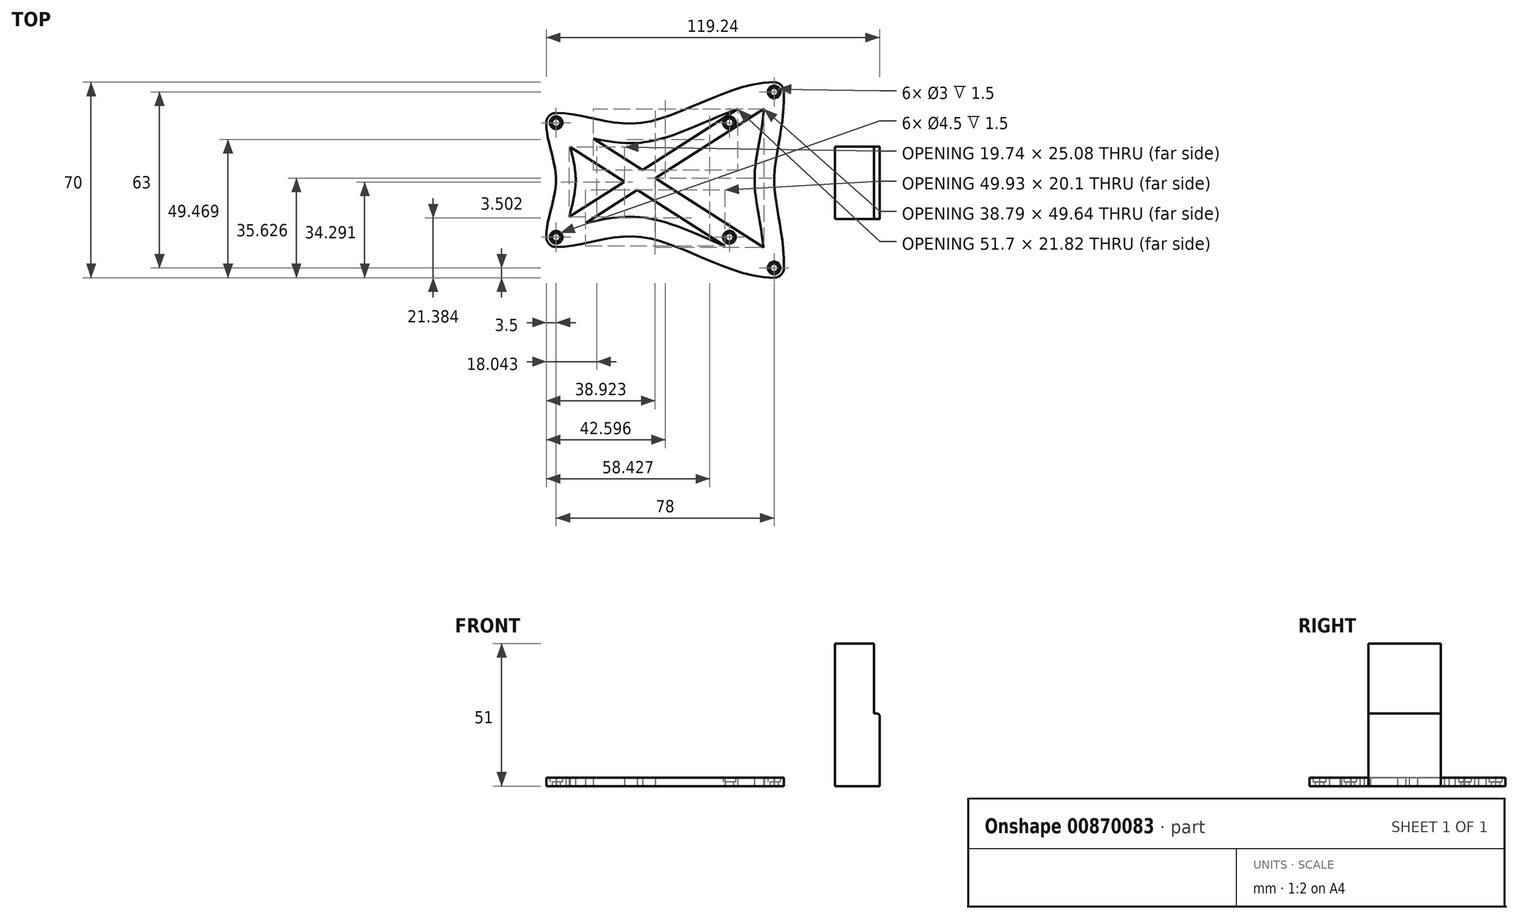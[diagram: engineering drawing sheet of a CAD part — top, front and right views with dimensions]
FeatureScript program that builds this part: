
annotation { "Feature Type Name" : "Feature", "Feature Type Description" : "" }
export const myFeature = defineFeature(function(context is Context, id is Id, definition is map)
    precondition{}
    {
        {
            var Q0;
            Q0=qCreatedBy(makeId("Top.planeOp"),FACE);
            var sketch = newSketch(context, id + "F0", { "sketchPlane" : qUnion([Q0])});
            skPoint(sketch, "E0.0.midPoint", {"position": v(0, 58.75) * mm});
            skLineSegment(sketch, "E1", {"start": v(-41.54, 41.54) * mm, "end": v(-31.58, 51.5) * mm});
            skLineSegment(sketch, "E2", {"start": v(-41.54, 41.54) * mm, "end": v(-51.5, 31.58) * mm});
            skPoint(sketch, "E3.center", {"position": v(0, 0) * mm});
            skLineSegment(sketch, "E4", {"start": v(0, 52.86) * mm, "end": v(0, 47.36) * mm, "construction": true});
            skArc(sketch, "E5.1.0", {"start": v(-52.21, -28.46) * mm, "mid": v(-47.36, 0) * mm, "end": v(-52.21, 28.46) * mm});
            skArc(sketch, "E6.1.0", {"start": v(28.46, -52.21) * mm, "mid": v(0, -47.36) * mm, "end": v(-28.46, -52.21) * mm});
            skArc(sketch, "E6.2.0", {"start": v(52.21, 28.46) * mm, "mid": v(47.36, 0) * mm, "end": v(52.21, -28.46) * mm});
            skArc(sketch, "E6.3.0", {"start": v(-28.46, 52.21) * mm, "mid": v(0, 47.36) * mm, "end": v(28.46, 52.21) * mm});
            skLineSegment(sketch, "E7.1.0", {"start": v(-41.54, -41.54) * mm, "end": v(-51.5, -31.58) * mm});
            skLineSegment(sketch, "E7.1.1", {"start": v(-41.54, -41.54) * mm, "end": v(-31.58, -51.5) * mm});
            skLineSegment(sketch, "E7.2.0", {"start": v(41.54, -41.54) * mm, "end": v(31.58, -51.5) * mm});
            skLineSegment(sketch, "E7.2.1", {"start": v(41.54, -41.54) * mm, "end": v(51.5, -31.58) * mm});
            skLineSegment(sketch, "E7.3.0", {"start": v(41.54, 41.54) * mm, "end": v(51.5, 31.58) * mm});
            skLineSegment(sketch, "E7.3.1", {"start": v(41.54, 41.54) * mm, "end": v(31.58, 51.5) * mm});
            skPoint(sketch, "E8.visualSharp", {"position": v(-52.86, 30.23) * mm});
            skArc(sketch, "E8.filletArc", {"start": v(-51.5, 31.58) * mm, "mid": v(-52.3, 30.12) * mm, "end": v(-52.21, 28.46) * mm});
            skPoint(sketch, "E9.visualSharp", {"position": v(-30.23, 52.86) * mm});
            skArc(sketch, "E9.filletArc", {"start": v(-28.46, 52.21) * mm, "mid": v(-30.12, 52.3) * mm, "end": v(-31.58, 51.5) * mm});
            skPoint(sketch, "E10.visualSharp", {"position": v(30.23, 52.86) * mm});
            skArc(sketch, "E10.filletArc", {"start": v(31.58, 51.5) * mm, "mid": v(30.12, 52.3) * mm, "end": v(28.46, 52.21) * mm});
            skPoint(sketch, "E11.visualSharp", {"position": v(52.86, 30.23) * mm});
            skArc(sketch, "E11.filletArc", {"start": v(52.21, 28.46) * mm, "mid": v(52.3, 30.12) * mm, "end": v(51.5, 31.58) * mm});
            skPoint(sketch, "E12.visualSharp", {"position": v(52.86, -30.23) * mm});
            skArc(sketch, "E12.filletArc", {"start": v(51.5, -31.58) * mm, "mid": v(52.3, -30.12) * mm, "end": v(52.21, -28.46) * mm});
            skPoint(sketch, "E13.visualSharp", {"position": v(30.23, -52.86) * mm});
            skArc(sketch, "E13.filletArc", {"start": v(28.46, -52.21) * mm, "mid": v(30.12, -52.3) * mm, "end": v(31.58, -51.5) * mm});
            skPoint(sketch, "E14.visualSharp", {"position": v(-30.23, -52.86) * mm});
            skArc(sketch, "E14.filletArc", {"start": v(-31.58, -51.5) * mm, "mid": v(-30.12, -52.3) * mm, "end": v(-28.46, -52.21) * mm});
            skPoint(sketch, "E15.visualSharp", {"position": v(-52.86, -30.23) * mm});
            skArc(sketch, "E15.filletArc", {"start": v(-52.21, -28.46) * mm, "mid": v(-52.3, -30.12) * mm, "end": v(-51.5, -31.58) * mm});
            skSolve(sketch);
        }
        {
            var Q0;
            Q0=makeQuery(id+"F0.imprint","IMPRINT",FACE,{"disambiguationData":[TD([[makeQuery(id+"F0.imprint","IMPRINT",EDGE,{"derivedFrom":sQuery(id+"F0.wireOp",EDGE,"E1")}),-1.0]])]});
            var sketch = newSketch(context, id + "F1", { "sketchPlane" : qUnion([Q0])});
            skLineSegment(sketch, "E16.bottom", {"start": v(92.64, 11.55) * mm, "end": v(108.64, 11.55) * mm});
            skLineSegment(sketch, "E16.top", {"start": v(92.64, -14.45) * mm, "end": v(108.64, -14.45) * mm});
            skLineSegment(sketch, "E16.left", {"start": v(92.64, 11.55) * mm, "end": v(92.64, -14.45) * mm});
            skLineSegment(sketch, "E16.right", {"start": v(108.64, 11.55) * mm, "end": v(108.64, -14.45) * mm});
            skSolve(sketch);
        }
        {
            var Q0;
            Q0=makeQuery(id+"F1.imprint","IMPRINT",FACE,{"disambiguationData":[TD([[makeQuery(id+"F1.imprint","IMPRINT",EDGE,{"derivedFrom":sQuery(id+"F1.wireOp",EDGE,"E16.bottom")}),-1.0]])]});
            extrude(context, id + "F2", {"entities" : qUnion([Q0]), "depth" : 26 * mm, "offsetDistance" : 25 * mm});
        }
        {
            var Q0;
            Q0=makeQuery(id+"F2.opExtrude","CAP_FACE",FACE,{"disambiguationData":[OSD([sQuery(id+"F1.wireOp",EDGE,"E16.bottom"),sQuery(id+"F1.wireOp",EDGE,"E16.top"),sQuery(id+"F1.wireOp",EDGE,"E16.left"),sQuery(id+"F1.wireOp",EDGE,"E16.right")])],"isStart":false});
            var sketch = newSketch(context, id + "F3", { "sketchPlane" : qUnion([Q0])});
            skLineSegment(sketch, "E17.bottom", {"start": v(92.64, 11.55) * mm, "end": v(106.64, 11.55) * mm});
            skLineSegment(sketch, "E17.top", {"start": v(92.64, -14.45) * mm, "end": v(106.64, -14.45) * mm});
            skLineSegment(sketch, "E17.left", {"start": v(92.64, 11.55) * mm, "end": v(92.64, -14.45) * mm});
            skLineSegment(sketch, "E17.right", {"start": v(106.64, 11.55) * mm, "end": v(106.64, -14.45) * mm});
            skSolve(sketch);
        }
        {
            var Q0;
            Q0=makeQuery(id+"F3.imprint","IMPRINT",FACE,{"disambiguationData":[TD([[makeQuery(id+"F3.imprint","IMPRINT",EDGE,{"derivedFrom":sQuery(id+"F3.wireOp",EDGE,"E17.bottom")}),-1.0]])]});
            extrude(context, id + "F4", {"entities" : qUnion([Q0]), "operationType" : NewBodyOperationType.ADD, "depth" : 25 * mm, "offsetDistance" : 25 * mm});
        }
        {
            var Q0;
            Q0=makeQuery(id+"F2.opExtrude","CAP_EDGE",EDGE,{"disambiguationData":[OSD([sQuery(id+"F1.wireOp",EDGE,"E16.right")])],"isStart":false});
            var Q1;
            Q1=makeQuery(id+"F4.opExtrude","CAP_EDGE",EDGE,{"disambiguationData":[OSD([sQuery(id+"F3.wireOp",EDGE,"E17.right")])],"isStart":true});
            fillet(context, id + "F5", {"entities" : qUnion([Q0, Q1]), "tangentPropagation" : true, "radius" : 1 * mm, "defaultsChanged" : true, "vertexSettings" : [], "allowEdgeOverflow" : false});
        }
        {
            var Q0;
            Q0=qCreatedBy(makeId("Top.planeOp"),FACE);
            var sketch = newSketch(context, id + "F6", { "sketchPlane" : qUnion([Q0])});
            skLineSegment(sketch, "E18.bottom", {"start": v(70.9, 31.08) * mm, "end": v(54.9, 31.08) * mm, "construction": true});
            skLineSegment(sketch, "E18.top", {"start": v(70.9, -31.92) * mm, "end": v(54.9, -31.92) * mm});
            skLineSegment(sketch, "E18.left", {"start": v(70.9, 31.08) * mm, "end": v(70.9, -31.92) * mm, "construction": true});
            skLineSegment(sketch, "E18.right", {"start": v(54.9, 31.08) * mm, "end": v(54.9, -31.92) * mm, "construction": true});
            skLineSegment(sketch, "E19", {"start": v(54.9, -31.92) * mm, "end": v(54.9, -20.92) * mm, "construction": true});
            skLineSegment(sketch, "E20", {"start": v(54.9, 31.08) * mm, "end": v(54.9, 20.08) * mm, "construction": true});
            skCircle(sketch, "E21", {"center": v(70.9, 31.08) * mm, "radius": 1.5 * mm});
            skCircle(sketch, "E22", {"center": v(70.9, 31.08) * mm, "radius": 2.25 * mm});
            skCircle(sketch, "E23", {"center": v(54.9, 20.08) * mm, "radius": 1.5 * mm});
            skCircle(sketch, "E24", {"center": v(54.9, 20.08) * mm, "radius": 2.25 * mm});
            skCircle(sketch, "E25", {"center": v(54.9, -20.92) * mm, "radius": 1.5 * mm});
            skCircle(sketch, "E26", {"center": v(54.9, -20.92) * mm, "radius": 2.25 * mm});
            skCircle(sketch, "E27", {"center": v(70.9, -31.92) * mm, "radius": 1.5 * mm});
            skCircle(sketch, "E28", {"center": v(70.9, -31.92) * mm, "radius": 2.25 * mm});
            skCircle(sketch, "E29", {"center": v(70.9, 31.08) * mm, "radius": 3.5 * mm});
            skCircle(sketch, "E30", {"center": v(70.9, -31.92) * mm, "radius": 3.5 * mm});
            skFitSpline(sketch, "E31", {"points": [v(74.4, 31.08) * mm, v(70.9, -0.42) * mm, v(74.4, -31.92) * mm], "startDerivative": vector(0, -88.08) * mm, "endDerivative": vector(0, -81.88) * mm});
            skLineSegment(sketch, "E32.bottom", {"start": v(54.9, 20.08) * mm, "end": v(-7.1, 20.08) * mm, "construction": true});
            skLineSegment(sketch, "E32.top", {"start": v(54.9, -20.92) * mm, "end": v(-7.1, -20.92) * mm, "construction": true});
            skLineSegment(sketch, "E32.right", {"start": v(-7.1, 20.08) * mm, "end": v(-7.1, -20.92) * mm, "construction": true});
            skCircle(sketch, "E33", {"center": v(-7.1, 20.08) * mm, "radius": 1.5 * mm});
            skCircle(sketch, "E34", {"center": v(-7.1, -20.92) * mm, "radius": 1.5 * mm});
            skCircle(sketch, "E35", {"center": v(-7.1, 20.08) * mm, "radius": 2.25 * mm});
            skCircle(sketch, "E36", {"center": v(-7.1, -20.92) * mm, "radius": 2.25 * mm});
            skCircle(sketch, "E37", {"center": v(-7.1, 20.08) * mm, "radius": 3.5 * mm});
            skCircle(sketch, "E38", {"center": v(-7.1, -20.92) * mm, "radius": 3.5 * mm});
            skFitSpline(sketch, "E39", {"points": [v(-10.6, 20.08) * mm, v(-7.1, -0.42) * mm, v(-10.6, -20.92) * mm], "startDerivative": vector(0, -42.32) * mm, "endDerivative": vector(0, -42.32) * mm});
            skFitSpline(sketch, "E40", {"points": [v(-7.1, -24.42) * mm, v(23.9, -20.92) * mm, v(70.9, -35.42) * mm], "startDerivative": vector(67.67, 0) * mm, "endDerivative": vector(86.23, 0) * mm});
            skFitSpline(sketch, "E41", {"points": [v(-7.1, 23.58) * mm, v(23.9, 20.08) * mm, v(70.9, 34.58) * mm], "startDerivative": vector(68.47, 0) * mm, "endDerivative": vector(86.23, 0) * mm});
            skLineSegment(sketch, "E42", {"start": v(-7.1, -20.92) * mm, "end": v(2.9, -20.92) * mm, "construction": true});
            skLineSegment(sketch, "E43", {"start": v(2.9, -20.92) * mm, "end": v(2.9, 20.08) * mm, "construction": true});
            skFitSpline(sketch, "E44.0", {"points": [v(-7.1, 16.58) * mm, v(-6.55, 16.58) * mm, v(-5.44, 16.54) * mm, v(-3.7, 16.38) * mm, v(-1.87, 16.12) * mm, v(0.04, 15.77) * mm, v(2.04, 15.36) * mm, v(4.12, 14.9) * mm, v(6.3, 14.43) * mm, v(8.56, 13.96) * mm, v(10.93, 13.53) * mm, v(13.4, 13.16) * mm, v(15.54, 12.93) * mm, v(17.31, 12.82) * mm, v(18.67, 12.77) * mm, v(20.05, 12.77) * mm, v(21.45, 12.82) * mm, v(22.64, 12.9) * mm, v(23.6, 13) * mm, v(24.2, 13.06) * mm, v(24.7, 13.12) * mm, v(25.18, 13.2) * mm, v(25.8, 13.29) * mm, v(26.52, 13.41) * mm, v(27.48, 13.6) * mm, v(28.68, 13.86) * mm, v(30.1, 14.22) * mm, v(31.52, 14.62) * mm, v(33.39, 15.19) * mm, v(35.7, 15.98) * mm, v(38.45, 17.01) * mm, v(41.17, 18.11) * mm, v(43.87, 19.25) * mm, v(47.44, 20.78) * mm, v(51.84, 22.66) * mm, v(56.13, 24.35) * mm, v(59.46, 25.5) * mm, v(61.9, 26.22) * mm, v(64.28, 26.82) * mm, v(66.58, 27.25) * mm, v(68.8, 27.52) * mm, v(70.2, 27.58) * mm, v(70.9, 27.58) * mm]});
            skFitSpline(sketch, "E45.0", {"points": [v(-7.1, -17.42) * mm, v(-6.56, -17.42) * mm, v(-5.46, -17.38) * mm, v(-3.74, -17.21) * mm, v(-1.92, -16.95) * mm, v(-0.02, -16.6) * mm, v(1.97, -16.2) * mm, v(4.06, -15.74) * mm, v(6.24, -15.27) * mm, v(8.51, -14.8) * mm, v(10.89, -14.36) * mm, v(13.36, -14) * mm, v(15.52, -13.77) * mm, v(17.3, -13.66) * mm, v(18.65, -13.61) * mm, v(20.03, -13.6) * mm, v(21.44, -13.65) * mm, v(22.63, -13.73) * mm, v(23.6, -13.83) * mm, v(24.2, -13.9) * mm, v(24.69, -13.96) * mm, v(25.18, -14.03) * mm, v(25.79, -14.12) * mm, v(26.52, -14.25) * mm, v(27.48, -14.44) * mm, v(28.68, -14.7) * mm, v(30.11, -15.06) * mm, v(31.53, -15.45) * mm, v(33.4, -16.02) * mm, v(35.72, -16.81) * mm, v(38.47, -17.85) * mm, v(41.2, -18.95) * mm, v(43.9, -20.09) * mm, v(47.46, -21.62) * mm, v(51.86, -23.5) * mm, v(56.14, -25.19) * mm, v(59.47, -26.33) * mm, v(61.9, -27.06) * mm, v(64.28, -27.65) * mm, v(66.58, -28.09) * mm, v(68.8, -28.36) * mm, v(70.2, -28.42) * mm, v(70.9, -28.42) * mm]});
            skFitSpline(sketch, "E46.0", {"points": [v(-3.6, 20.08) * mm, v(-3.6, 19.79) * mm, v(-3.58, 19.18) * mm, v(-3.5, 18.22) * mm, v(-3.37, 17.22) * mm, v(-3.12, 15.81) * mm, v(-2.7, 13.93) * mm, v(-2.18, 11.9) * mm, v(-1.74, 10.16) * mm, v(-1.4, 8.82) * mm, v(-1.07, 7.42) * mm, v(-0.77, 5.98) * mm, v(-0.54, 4.72) * mm, v(-0.4, 3.69) * mm, v(-0.3, 2.9) * mm, v(-0.2, 2.1) * mm, v(-0.16, 1.4) * mm, v(-0.13, 0.85) * mm, v(-0.11, 0.43) * mm, v(-0.1, 0.08) * mm, v(-0.1, -0.2) * mm, v(-0.1, -0.42) * mm, v(-0.1, -0.63) * mm, v(-0.1, -0.92) * mm, v(-0.11, -1.27) * mm, v(-0.13, -1.69) * mm, v(-0.16, -2.24) * mm, v(-0.2, -2.93) * mm, v(-0.3, -3.73) * mm, v(-0.4, -4.52) * mm, v(-0.54, -5.56) * mm, v(-0.77, -6.81) * mm, v(-1.08, -8.26) * mm, v(-1.4, -9.66) * mm, v(-1.74, -11) * mm, v(-2.18, -12.73) * mm, v(-2.7, -14.77) * mm, v(-3.12, -16.65) * mm, v(-3.37, -18.05) * mm, v(-3.5, -19.06) * mm, v(-3.58, -20.02) * mm, v(-3.6, -20.62) * mm, v(-3.6, -20.92) * mm]});
            skFitSpline(sketch, "E47.0", {"points": [v(67.4, 31.08) * mm, v(67.4, 29.39) * mm, v(67.3, 26.2) * mm, v(66.92, 21.9) * mm, v(66.39, 17.96) * mm, v(65.87, 14.89) * mm, v(65.43, 12.5) * mm, v(65.11, 10.7) * mm, v(64.8, 8.92) * mm, v(64.52, 7.13) * mm, v(64.3, 5.6) * mm, v(64.17, 4.38) * mm, v(64.07, 3.44) * mm, v(64, 2.5) * mm, v(63.95, 1.7) * mm, v(63.93, 1.05) * mm, v(63.91, 0.57) * mm, v(63.9, 0.16) * mm, v(63.9, -0.17) * mm, v(63.9, -0.42) * mm, v(63.9, -0.67) * mm, v(63.9, -1) * mm, v(63.91, -1.4) * mm, v(63.93, -1.9) * mm, v(63.95, -2.54) * mm, v(64, -3.35) * mm, v(64.07, -4.3) * mm, v(64.16, -5.26) * mm, v(64.3, -6.51) * mm, v(64.51, -8.07) * mm, v(64.8, -9.93) * mm, v(65.1, -11.77) * mm, v(65.43, -13.62) * mm, v(65.86, -16.1) * mm, v(66.39, -19.26) * mm, v(66.92, -23.2) * mm, v(67.3, -27.38) * mm, v(67.4, -30.36) * mm, v(67.4, -31.92) * mm]});
            skLineSegment(sketch, "E48", {"start": v(-3.2, -17.13) * mm, "end": v(65.83, 27.1) * mm, "construction": true});
            skArc(sketch, "E49.0.startCap", {"start": v(-1.85, -19.24) * mm, "mid": v(-5.3, -18.48) * mm, "end": v(-4.55, -15.03) * mm, "construction": true});
            skArc(sketch, "E49.0.endCap", {"start": v(64.48, 29.2) * mm, "mid": v(67.93, 28.45) * mm, "end": v(67.17, 25) * mm});
            skLineSegment(sketch, "E49.0.left", {"start": v(-4.55, -15.03) * mm, "end": v(64.48, 29.2) * mm});
            skLineSegment(sketch, "E49.0.right", {"start": v(-1.85, -19.24) * mm, "end": v(67.17, 25) * mm});
            skLineSegment(sketch, "E50", {"start": v(-3.2, 16.3) * mm, "end": v(65.75, -27.93) * mm, "construction": true});
            skArc(sketch, "E51.0.startCap", {"start": v(-5.1, 13.36) * mm, "mid": v(-6.15, 18.2) * mm, "end": v(-1.31, 19.25) * mm, "construction": true});
            skArc(sketch, "E51.0.endCap", {"start": v(67.64, -24.98) * mm, "mid": v(68.7, -29.81) * mm, "end": v(63.87, -30.87) * mm, "construction": true});
            skLineSegment(sketch, "E51.0.left", {"start": v(-1.31, 19.25) * mm, "end": v(67.64, -24.98) * mm});
            skLineSegment(sketch, "E51.0.right", {"start": v(-5.1, 13.36) * mm, "end": v(63.87, -30.87) * mm});
            skSolve(sketch);
        }
        {
            var Q0;
            {var subQ5=sQuery(id+"F6.wireOp",EDGE,"E39");Q0=makeQuery(id+"F6.imprint","IMPRINT",FACE,{"disambiguationData":[TD([[makeQuery(id+"F6.imprint","IMPRINT",EDGE,{"derivedFrom":subQ5}),1.0]])]});}
            var Q1;
            Q1=makeQuery(id+"F6.imprint","IMPRINT",FACE,{"disambiguationData":[TD([[makeQuery(id+"F6.imprint","IMPRINT",EDGE,{"derivedFrom":sQuery(id+"F6.wireOp",EDGE,"E36")}),-1.0]])]});
            var Q2;
            Q2=makeQuery(id+"F6.imprint","IMPRINT",FACE,{"disambiguationData":[TD([[makeQuery(id+"F6.imprint","IMPRINT",EDGE,{"derivedFrom":sQuery(id+"F6.wireOp",EDGE,"E34")}),-1.0]])]});
            var Q3;
            Q3=makeQuery(id+"F6.imprint","IMPRINT",FACE,{"disambiguationData":[TD([[makeQuery(id+"F6.imprint","IMPRINT",EDGE,{"derivedFrom":sQuery(id+"F6.wireOp",EDGE,"E27")}),-1.0]])]});
            var Q4;
            Q4=makeQuery(id+"F6.imprint","IMPRINT",FACE,{"disambiguationData":[TD([[makeQuery(id+"F6.imprint","IMPRINT",EDGE,{"derivedFrom":sQuery(id+"F6.wireOp",EDGE,"E28")}),-1.0]])]});
            var Q5;
            Q5=makeQuery(id+"F6.imprint","IMPRINT",FACE,{"disambiguationData":[TD([[makeQuery(id+"F6.imprint","IMPRINT",EDGE,{"derivedFrom":sQuery(id+"F6.wireOp",EDGE,"E25")}),-1.0]])]});
            var Q6;
            Q6=makeQuery(id+"F6.imprint","IMPRINT",FACE,{"disambiguationData":[TD([[makeQuery(id+"F6.imprint","IMPRINT",EDGE,{"derivedFrom":sQuery(id+"F6.wireOp",EDGE,"E22")}),-1.0]])]});
            var Q7;
            Q7=makeQuery(id+"F6.imprint","IMPRINT",FACE,{"disambiguationData":[TD([[makeQuery(id+"F6.imprint","IMPRINT",EDGE,{"derivedFrom":sQuery(id+"F6.wireOp",EDGE,"E21")}),-1.0]])]});
            var Q8;
            Q8=makeQuery(id+"F6.imprint","IMPRINT",FACE,{"disambiguationData":[TD([[makeQuery(id+"F6.imprint","IMPRINT",EDGE,{"derivedFrom":sQuery(id+"F6.wireOp",EDGE,"E33")}),-1.0]])]});
            var Q9;
            Q9=makeQuery(id+"F6.imprint","IMPRINT",FACE,{"disambiguationData":[TD([[makeQuery(id+"F6.imprint","IMPRINT",EDGE,{"derivedFrom":sQuery(id+"F6.wireOp",EDGE,"E35")}),-1.0]])]});
            var Q10;
            Q10=makeQuery(id+"F6.imprint","IMPRINT",FACE,{"disambiguationData":[TD([[makeQuery(id+"F6.imprint","IMPRINT",EDGE,{"derivedFrom":sQuery(id+"F6.wireOp",EDGE,"E23")}),-1.0]])]});
            var Q11;
            {var subQ4=sQuery(id+"F6.wireOp",EDGE,"E40");var subQ5=sQuery(id+"F6.wireOp",EDGE,"E30");var subQ6=makeQuery(id+"F6.imprint","INTERSECT",VERTEX,{"derivedFrom":[subQ5,subQ4]});Q11=makeQuery(id+"F6.imprint","IMPRINT",FACE,{"disambiguationData":[TD([[makeQuery(id+"F6.imprint","IMPRINT",EDGE,{"disambiguationData":[TD([[subQ6,1.0]])],"derivedFrom":subQ5}),-1.0]])]});}
            var Q12;
            {var subQ4=sQuery(id+"F6.wireOp",EDGE,"E40");var subQ8=sQuery(id+"F6.wireOp",EDGE,"E38");var subQ9=makeQuery(id+"F6.imprint","INTERSECT",VERTEX,{"derivedFrom":[subQ8,subQ4]});Q12=makeQuery(id+"F6.imprint","IMPRINT",FACE,{"disambiguationData":[TD([[makeQuery(id+"F6.imprint","IMPRINT",EDGE,{"disambiguationData":[TD([[subQ9,-1.0]])],"derivedFrom":subQ8}),-1.0]])]});}
            var Q13;
            {var subQ0=sQuery(id+"F6.wireOp",EDGE,"E49.0.left");var subQ1=sQuery(id+"F6.wireOp",EDGE,"9af11305-70bc-4bd8-85a8-762773eb8b53.0.left");var subQ2=makeQuery(id+"F6.imprint","INTERSECT",VERTEX,{"derivedFrom":[subQ1,subQ0]});Q13=makeQuery(id+"F6.imprint","IMPRINT",FACE,{"disambiguationData":[TD([[makeQuery(id+"F6.imprint","IMPRINT",EDGE,{"disambiguationData":[TD([[subQ2,-1.0]])],"derivedFrom":subQ1}),-1.0]])]});}
            var Q14;
            {var subQ7=sQuery(id+"F6.wireOp",EDGE,"9af11305-70bc-4bd8-85a8-762773eb8b53.0.right");var subQ9=sQuery(id+"F6.wireOp",EDGE,"E26");var subQ11=makeQuery(id+"F6.imprint","INTERSECT",VERTEX,{"disambiguationData":[OD(0.0)],"derivedFrom":[subQ9,subQ7]});Q14=makeQuery(id+"F6.imprint","IMPRINT",FACE,{"disambiguationData":[TD([[makeQuery(id+"F6.imprint","IMPRINT",EDGE,{"disambiguationData":[TD([[subQ11,1.0]])],"derivedFrom":subQ9}),-1.0]])]});}
            var Q15;
            {var subQ5=sQuery(id+"F6.wireOp",EDGE,"E31");Q15=makeQuery(id+"F6.imprint","IMPRINT",FACE,{"disambiguationData":[TD([[makeQuery(id+"F6.imprint","IMPRINT",EDGE,{"derivedFrom":subQ5}),-1.0]])]});}
            var Q16;
            {var subQ0=sQuery(id+"F6.wireOp",EDGE,"E45.0");var subQ1=sQuery(id+"F6.wireOp",EDGE,"E30");var subQ2=makeQuery(id+"F6.imprint","INTERSECT",VERTEX,{"derivedFrom":[subQ1,subQ0]});Q16=makeQuery(id+"F6.imprint","IMPRINT",FACE,{"disambiguationData":[TD([[makeQuery(id+"F6.imprint","IMPRINT",EDGE,{"disambiguationData":[TD([[subQ2,-1.0]])],"derivedFrom":subQ1}),-1.0]])]});}
            var Q17;
            {var subQ6=sQuery(id+"F6.wireOp",EDGE,"E41");var subQ7=sQuery(id+"F6.wireOp",EDGE,"E29");var subQ8=makeQuery(id+"F6.imprint","INTERSECT",VERTEX,{"derivedFrom":[subQ7,subQ6]});Q17=makeQuery(id+"F6.imprint","IMPRINT",FACE,{"disambiguationData":[TD([[makeQuery(id+"F6.imprint","IMPRINT",EDGE,{"disambiguationData":[TD([[subQ8,-1.0]])],"derivedFrom":subQ7}),-1.0]])]});}
            var Q18;
            {var subQ0=sQuery(id+"F6.wireOp",EDGE,"E44.0");var subQ1=sQuery(id+"F6.wireOp",EDGE,"E29");var subQ2=makeQuery(id+"F6.imprint","INTERSECT",VERTEX,{"derivedFrom":[subQ1,subQ0]});Q18=makeQuery(id+"F6.imprint","IMPRINT",FACE,{"disambiguationData":[TD([[makeQuery(id+"F6.imprint","IMPRINT",EDGE,{"disambiguationData":[TD([[subQ2,1.0]])],"derivedFrom":subQ1}),-1.0]])]});}
            var Q19;
            {var subQ0=sQuery(id+"F6.wireOp",EDGE,"E49.0.right");var subQ1=sQuery(id+"F6.wireOp",EDGE,"9af11305-70bc-4bd8-85a8-762773eb8b53.0.left");var subQ2=makeQuery(id+"F6.imprint","INTERSECT",VERTEX,{"derivedFrom":[subQ1,subQ0]});Q19=makeQuery(id+"F6.imprint","IMPRINT",FACE,{"disambiguationData":[TD([[makeQuery(id+"F6.imprint","IMPRINT",EDGE,{"disambiguationData":[TD([[subQ2,-1.0]])],"derivedFrom":subQ1}),-1.0]])]});}
            var Q20;
            {var subQ0=sQuery(id+"F6.wireOp",EDGE,"E49.0.left");var subQ1=sQuery(id+"F6.wireOp",EDGE,"9af11305-70bc-4bd8-85a8-762773eb8b53.0.left");var subQ2=makeQuery(id+"F6.imprint","INTERSECT",VERTEX,{"derivedFrom":[subQ1,subQ0]});Q20=makeQuery(id+"F6.imprint","IMPRINT",FACE,{"disambiguationData":[TD([[makeQuery(id+"F6.imprint","IMPRINT",EDGE,{"disambiguationData":[TD([[subQ2,-1.0]])],"derivedFrom":subQ1}),1.0]])]});}
            var Q21;
            {var subQ4=sQuery(id+"F6.wireOp",EDGE,"E37");var subQ6=sQuery(id+"F6.wireOp",EDGE,"E41");var subQ7=makeQuery(id+"F6.imprint","INTERSECT",VERTEX,{"derivedFrom":[subQ4,subQ6]});Q21=makeQuery(id+"F6.imprint","IMPRINT",FACE,{"disambiguationData":[TD([[makeQuery(id+"F6.imprint","IMPRINT",EDGE,{"disambiguationData":[TD([[subQ7,1.0]])],"derivedFrom":subQ4}),-1.0]])]});}
            var Q22;
            {var subQ0=sQuery(id+"F6.wireOp",EDGE,"E44.0");var subQ1=sQuery(id+"F6.wireOp",EDGE,"E37");var subQ2=makeQuery(id+"F6.imprint","INTERSECT",VERTEX,{"derivedFrom":[subQ1,subQ0]});Q22=makeQuery(id+"F6.imprint","IMPRINT",FACE,{"disambiguationData":[TD([[makeQuery(id+"F6.imprint","IMPRINT",EDGE,{"disambiguationData":[TD([[subQ2,-1.0]])],"derivedFrom":subQ1}),-1.0]])]});}
            var Q23;
            {var subQ0=sQuery(id+"F6.wireOp",EDGE,"E45.0");var subQ1=sQuery(id+"F6.wireOp",EDGE,"E38");var subQ2=makeQuery(id+"F6.imprint","INTERSECT",VERTEX,{"derivedFrom":[subQ1,subQ0]});Q23=makeQuery(id+"F6.imprint","IMPRINT",FACE,{"disambiguationData":[TD([[makeQuery(id+"F6.imprint","IMPRINT",EDGE,{"disambiguationData":[TD([[subQ2,1.0]])],"derivedFrom":subQ1}),-1.0]])]});}
            var Q24;
            {var subQ3=sQuery(id+"F6.wireOp",EDGE,"E45.0");var subQ7=sQuery(id+"F6.wireOp",EDGE,"E49.0.right");var subQ9=makeQuery(id+"F6.imprint","INTERSECT",VERTEX,{"derivedFrom":[subQ3,subQ7]});Q24=makeQuery(id+"F6.imprint","IMPRINT",FACE,{"disambiguationData":[TD([[makeQuery(id+"F6.imprint","IMPRINT",EDGE,{"disambiguationData":[TD([[subQ9,1.0]])],"derivedFrom":subQ3}),1.0]])]});}
            var Q25;
            {var subQ0=sQuery(id+"F6.wireOp",EDGE,"E51.0.right");var subQ1=sQuery(id+"F6.wireOp",EDGE,"E49.0.right");var subQ2=makeQuery(id+"F6.imprint","INTERSECT",VERTEX,{"derivedFrom":[subQ1,subQ0]});Q25=makeQuery(id+"F6.imprint","IMPRINT",FACE,{"disambiguationData":[TD([[makeQuery(id+"F6.imprint","IMPRINT",EDGE,{"disambiguationData":[TD([[subQ2,-1.0]])],"derivedFrom":subQ1}),-1.0]])]});}
            var Q26;
            {var subQ0=sQuery(id+"F6.wireOp",EDGE,"E51.0.right");var subQ1=sQuery(id+"F6.wireOp",EDGE,"E49.0.left");var subQ2=makeQuery(id+"F6.imprint","INTERSECT",VERTEX,{"derivedFrom":[subQ1,subQ0]});Q26=makeQuery(id+"F6.imprint","IMPRINT",FACE,{"disambiguationData":[TD([[makeQuery(id+"F6.imprint","IMPRINT",EDGE,{"disambiguationData":[TD([[subQ2,-1.0]])],"derivedFrom":subQ1}),-1.0]])]});}
            var Q27;
            {var subQ3=sQuery(id+"F6.wireOp",EDGE,"E51.0.left");var subQ5=sQuery(id+"F6.wireOp",EDGE,"E44.0");var subQ6=makeQuery(id+"F6.imprint","INTERSECT",VERTEX,{"derivedFrom":[subQ5,subQ3]});Q27=makeQuery(id+"F6.imprint","IMPRINT",FACE,{"disambiguationData":[TD([[makeQuery(id+"F6.imprint","IMPRINT",EDGE,{"disambiguationData":[TD([[subQ6,1.0]])],"derivedFrom":subQ5}),-1.0]])]});}
            var Q28;
            {var subQ0=sQuery(id+"F6.wireOp",EDGE,"E51.0.left");var subQ1=sQuery(id+"F6.wireOp",EDGE,"E49.0.left");var subQ2=makeQuery(id+"F6.imprint","INTERSECT",VERTEX,{"derivedFrom":[subQ1,subQ0]});Q28=makeQuery(id+"F6.imprint","IMPRINT",FACE,{"disambiguationData":[TD([[makeQuery(id+"F6.imprint","IMPRINT",EDGE,{"disambiguationData":[TD([[subQ2,-1.0]])],"derivedFrom":subQ1}),-1.0]])]});}
            var Q29;
            Q29=makeQuery(id+"F6.imprint","IMPRINT",FACE,{"disambiguationData":[TD([[makeQuery(id+"F6.imprint","IMPRINT",EDGE,{"derivedFrom":sQuery(id+"F6.wireOp",EDGE,"E24")}),-1.0]])]});
            var Q30;
            {var subQ0=sQuery(id+"F6.wireOp",EDGE,"E49.0.left");var subQ1=sQuery(id+"F6.wireOp",EDGE,"E44.0");var subQ2=makeQuery(id+"F6.imprint","INTERSECT",VERTEX,{"derivedFrom":[subQ1,subQ0]});Q30=makeQuery(id+"F6.imprint","IMPRINT",FACE,{"disambiguationData":[TD([[makeQuery(id+"F6.imprint","IMPRINT",EDGE,{"disambiguationData":[TD([[subQ2,-1.0]])],"derivedFrom":subQ1}),1.0]])]});}
            var Q31;
            {var subQ0=sQuery(id+"F6.wireOp",EDGE,"E47.0");var subQ1=sQuery(id+"F6.wireOp",EDGE,"E44.0");var subQ2=makeQuery(id+"F6.imprint","INTERSECT",VERTEX,{"derivedFrom":[subQ1,subQ0]});Q31=makeQuery(id+"F6.imprint","IMPRINT",FACE,{"disambiguationData":[TD([[makeQuery(id+"F6.imprint","IMPRINT",EDGE,{"disambiguationData":[TD([[subQ2,-1.0]])],"derivedFrom":subQ1}),-1.0]])]});}
            var Q32;
            {var subQ0=sQuery(id+"F6.wireOp",EDGE,"E47.0");var subQ1=sQuery(id+"F6.wireOp",EDGE,"E44.0");var subQ2=makeQuery(id+"F6.imprint","INTERSECT",VERTEX,{"derivedFrom":[subQ1,subQ0]});Q32=makeQuery(id+"F6.imprint","IMPRINT",FACE,{"disambiguationData":[TD([[makeQuery(id+"F6.imprint","IMPRINT",EDGE,{"disambiguationData":[TD([[subQ2,-1.0]])],"derivedFrom":subQ1}),1.0]])]});}
            extrude(context, id + "F7", {"entities" : qUnion([Q0, Q1, Q2, Q3, Q4, Q5, Q6, Q7, Q8, Q9, Q10, Q11, Q12, Q13, Q14, Q15, Q16, Q17, Q18, Q19, Q20, Q21, Q22, Q23, Q24, Q25, Q26, Q27, Q28, Q29, Q30, Q31, Q32]), "operationType" : NewBodyOperationType.ADD, "depth" : 1.5 * mm, "offsetDistance" : 25 * mm});
        }
        {
            var Q0;
            {var subQ5=sQuery(id+"F6.wireOp",EDGE,"E31");Q0=makeQuery(id+"F6.imprint","IMPRINT",FACE,{"disambiguationData":[TD([[makeQuery(id+"F6.imprint","IMPRINT",EDGE,{"derivedFrom":subQ5}),-1.0]])]});}
            var Q1;
            {var subQ0=sQuery(id+"F6.wireOp",EDGE,"E45.0");var subQ1=sQuery(id+"F6.wireOp",EDGE,"E30");var subQ2=makeQuery(id+"F6.imprint","INTERSECT",VERTEX,{"derivedFrom":[subQ1,subQ0]});Q1=makeQuery(id+"F6.imprint","IMPRINT",FACE,{"disambiguationData":[TD([[makeQuery(id+"F6.imprint","IMPRINT",EDGE,{"disambiguationData":[TD([[subQ2,-1.0]])],"derivedFrom":subQ1}),-1.0]])]});}
            var Q2;
            {var subQ4=sQuery(id+"F6.wireOp",EDGE,"E40");var subQ8=sQuery(id+"F6.wireOp",EDGE,"E30");var subQ9=makeQuery(id+"F6.imprint","INTERSECT",VERTEX,{"derivedFrom":[subQ8,subQ4]});Q2=makeQuery(id+"F6.imprint","IMPRINT",FACE,{"disambiguationData":[TD([[makeQuery(id+"F6.imprint","IMPRINT",EDGE,{"disambiguationData":[TD([[subQ9,1.0]])],"derivedFrom":subQ8}),-1.0]])]});}
            var Q3;
            Q3=makeQuery(id+"F6.imprint","IMPRINT",FACE,{"disambiguationData":[TD([[makeQuery(id+"F6.imprint","IMPRINT",EDGE,{"derivedFrom":sQuery(id+"F6.wireOp",EDGE,"E26")}),-1.0]])]});
            var Q4;
            Q4=makeQuery(id+"F6.imprint","IMPRINT",FACE,{"disambiguationData":[TD([[makeQuery(id+"F6.imprint","IMPRINT",EDGE,{"derivedFrom":sQuery(id+"F6.wireOp",EDGE,"E28")}),-1.0]])]});
            var Q5;
            {var subQ0=sQuery(id+"F6.wireOp",EDGE,"E44.0");var subQ1=sQuery(id+"F6.wireOp",EDGE,"E29");var subQ2=makeQuery(id+"F6.imprint","INTERSECT",VERTEX,{"derivedFrom":[subQ1,subQ0]});Q5=makeQuery(id+"F6.imprint","IMPRINT",FACE,{"disambiguationData":[TD([[makeQuery(id+"F6.imprint","IMPRINT",EDGE,{"disambiguationData":[TD([[subQ2,1.0]])],"derivedFrom":subQ1}),-1.0]])]});}
            var Q6;
            {var subQ0=sQuery(id+"F6.wireOp",EDGE,"E47.0");var subQ1=sQuery(id+"F6.wireOp",EDGE,"E44.0");var subQ2=makeQuery(id+"F6.imprint","INTERSECT",VERTEX,{"derivedFrom":[subQ1,subQ0]});Q6=makeQuery(id+"F6.imprint","IMPRINT",FACE,{"disambiguationData":[TD([[makeQuery(id+"F6.imprint","IMPRINT",EDGE,{"disambiguationData":[TD([[subQ2,-1.0]])],"derivedFrom":subQ1}),1.0]])]});}
            var Q7;
            {var subQ0=sQuery(id+"F6.wireOp",EDGE,"E47.0");var subQ1=sQuery(id+"F6.wireOp",EDGE,"E44.0");var subQ2=makeQuery(id+"F6.imprint","INTERSECT",VERTEX,{"derivedFrom":[subQ1,subQ0]});Q7=makeQuery(id+"F6.imprint","IMPRINT",FACE,{"disambiguationData":[TD([[makeQuery(id+"F6.imprint","IMPRINT",EDGE,{"disambiguationData":[TD([[subQ2,-1.0]])],"derivedFrom":subQ1}),-1.0]])]});}
            var Q8;
            {var subQ0=sQuery(id+"F6.wireOp",EDGE,"E49.0.left");var subQ1=sQuery(id+"F6.wireOp",EDGE,"E44.0");var subQ2=makeQuery(id+"F6.imprint","INTERSECT",VERTEX,{"derivedFrom":[subQ1,subQ0]});Q8=makeQuery(id+"F6.imprint","IMPRINT",FACE,{"disambiguationData":[TD([[makeQuery(id+"F6.imprint","IMPRINT",EDGE,{"disambiguationData":[TD([[subQ2,-1.0]])],"derivedFrom":subQ1}),1.0]])]});}
            var Q9;
            {var subQ1=sQuery(id+"F6.wireOp",EDGE,"E29");var subQ10=sQuery(id+"F6.wireOp",EDGE,"E41");var subQ11=makeQuery(id+"F6.imprint","INTERSECT",VERTEX,{"derivedFrom":[subQ1,subQ10]});Q9=makeQuery(id+"F6.imprint","IMPRINT",FACE,{"disambiguationData":[TD([[makeQuery(id+"F6.imprint","IMPRINT",EDGE,{"disambiguationData":[TD([[subQ11,-1.0]])],"derivedFrom":subQ1}),-1.0]])]});}
            var Q10;
            Q10=makeQuery(id+"F6.imprint","IMPRINT",FACE,{"disambiguationData":[TD([[makeQuery(id+"F6.imprint","IMPRINT",EDGE,{"derivedFrom":sQuery(id+"F6.wireOp",EDGE,"E22")}),-1.0]])]});
            var Q11;
            Q11=makeQuery(id+"F6.imprint","IMPRINT",FACE,{"disambiguationData":[TD([[makeQuery(id+"F6.imprint","IMPRINT",EDGE,{"derivedFrom":sQuery(id+"F6.wireOp",EDGE,"E24")}),-1.0]])]});
            var Q12;
            {var subQ0=sQuery(id+"F6.wireOp",EDGE,"E51.0.left");var subQ1=sQuery(id+"F6.wireOp",EDGE,"E49.0.left");var subQ2=makeQuery(id+"F6.imprint","INTERSECT",VERTEX,{"derivedFrom":[subQ1,subQ0]});Q12=makeQuery(id+"F6.imprint","IMPRINT",FACE,{"disambiguationData":[TD([[makeQuery(id+"F6.imprint","IMPRINT",EDGE,{"disambiguationData":[TD([[subQ2,-1.0]])],"derivedFrom":subQ1}),-1.0]])]});}
            var Q13;
            {var subQ4=sQuery(id+"F6.wireOp",EDGE,"E41");var subQ8=sQuery(id+"F6.wireOp",EDGE,"E37");var subQ9=makeQuery(id+"F6.imprint","INTERSECT",VERTEX,{"derivedFrom":[subQ8,subQ4]});Q13=makeQuery(id+"F6.imprint","IMPRINT",FACE,{"disambiguationData":[TD([[makeQuery(id+"F6.imprint","IMPRINT",EDGE,{"disambiguationData":[TD([[subQ9,1.0]])],"derivedFrom":subQ8}),-1.0]])]});}
            var Q14;
            {var subQ0=sQuery(id+"F6.wireOp",EDGE,"E51.0.right");var subQ1=sQuery(id+"F6.wireOp",EDGE,"E49.0.right");var subQ2=makeQuery(id+"F6.imprint","INTERSECT",VERTEX,{"derivedFrom":[subQ1,subQ0]});Q14=makeQuery(id+"F6.imprint","IMPRINT",FACE,{"disambiguationData":[TD([[makeQuery(id+"F6.imprint","IMPRINT",EDGE,{"disambiguationData":[TD([[subQ2,-1.0]])],"derivedFrom":subQ1}),-1.0]])]});}
            var Q15;
            {var subQ0=sQuery(id+"F6.wireOp",EDGE,"E51.0.left");var subQ1=sQuery(id+"F6.wireOp",EDGE,"E44.0");var subQ2=makeQuery(id+"F6.imprint","INTERSECT",VERTEX,{"derivedFrom":[subQ1,subQ0]});Q15=makeQuery(id+"F6.imprint","IMPRINT",FACE,{"disambiguationData":[TD([[makeQuery(id+"F6.imprint","IMPRINT",EDGE,{"disambiguationData":[TD([[subQ2,1.0]])],"derivedFrom":subQ1}),-1.0]])]});}
            var Q16;
            {var subQ0=sQuery(id+"F6.wireOp",EDGE,"E51.0.right");var subQ1=sQuery(id+"F6.wireOp",EDGE,"E49.0.left");var subQ2=makeQuery(id+"F6.imprint","INTERSECT",VERTEX,{"derivedFrom":[subQ1,subQ0]});Q16=makeQuery(id+"F6.imprint","IMPRINT",FACE,{"disambiguationData":[TD([[makeQuery(id+"F6.imprint","IMPRINT",EDGE,{"disambiguationData":[TD([[subQ2,-1.0]])],"derivedFrom":subQ1}),-1.0]])]});}
            var Q17;
            {var subQ4=sQuery(id+"F6.wireOp",EDGE,"E40");var subQ5=sQuery(id+"F6.wireOp",EDGE,"E38");var subQ6=makeQuery(id+"F6.imprint","INTERSECT",VERTEX,{"derivedFrom":[subQ5,subQ4]});Q17=makeQuery(id+"F6.imprint","IMPRINT",FACE,{"disambiguationData":[TD([[makeQuery(id+"F6.imprint","IMPRINT",EDGE,{"disambiguationData":[TD([[subQ6,-1.0]])],"derivedFrom":subQ5}),-1.0]])]});}
            var Q18;
            {var subQ5=sQuery(id+"F6.wireOp",EDGE,"E39");Q18=makeQuery(id+"F6.imprint","IMPRINT",FACE,{"disambiguationData":[TD([[makeQuery(id+"F6.imprint","IMPRINT",EDGE,{"derivedFrom":subQ5}),1.0]])]});}
            var Q19;
            Q19=makeQuery(id+"F6.imprint","IMPRINT",FACE,{"disambiguationData":[TD([[makeQuery(id+"F6.imprint","IMPRINT",EDGE,{"derivedFrom":sQuery(id+"F6.wireOp",EDGE,"E36")}),-1.0]])]});
            var Q20;
            {var subQ3=sQuery(id+"F6.wireOp",EDGE,"E45.0");var subQ5=sQuery(id+"F6.wireOp",EDGE,"E49.0.right");var subQ6=makeQuery(id+"F6.imprint","INTERSECT",VERTEX,{"derivedFrom":[subQ3,subQ5]});Q20=makeQuery(id+"F6.imprint","IMPRINT",FACE,{"disambiguationData":[TD([[makeQuery(id+"F6.imprint","IMPRINT",EDGE,{"disambiguationData":[TD([[subQ6,1.0]])],"derivedFrom":subQ3}),1.0]])]});}
            var Q21;
            {var subQ0=sQuery(id+"F6.wireOp",EDGE,"E44.0");var subQ1=sQuery(id+"F6.wireOp",EDGE,"E37");var subQ2=makeQuery(id+"F6.imprint","INTERSECT",VERTEX,{"derivedFrom":[subQ1,subQ0]});Q21=makeQuery(id+"F6.imprint","IMPRINT",FACE,{"disambiguationData":[TD([[makeQuery(id+"F6.imprint","IMPRINT",EDGE,{"disambiguationData":[TD([[subQ2,-1.0]])],"derivedFrom":subQ1}),-1.0]])]});}
            var Q22;
            Q22=makeQuery(id+"F6.imprint","IMPRINT",FACE,{"disambiguationData":[TD([[makeQuery(id+"F6.imprint","IMPRINT",EDGE,{"derivedFrom":sQuery(id+"F6.wireOp",EDGE,"E35")}),-1.0]])]});
            var Q23;
            {var subQ0=sQuery(id+"F6.wireOp",EDGE,"E45.0");var subQ1=sQuery(id+"F6.wireOp",EDGE,"E38");var subQ2=makeQuery(id+"F6.imprint","INTERSECT",VERTEX,{"derivedFrom":[subQ1,subQ0]});Q23=makeQuery(id+"F6.imprint","IMPRINT",FACE,{"disambiguationData":[TD([[makeQuery(id+"F6.imprint","IMPRINT",EDGE,{"disambiguationData":[TD([[subQ2,1.0]])],"derivedFrom":subQ1}),-1.0]])]});}
            extrude(context, id + "F8", {"entities" : qUnion([Q0, Q1, Q2, Q3, Q4, Q5, Q6, Q7, Q8, Q9, Q10, Q11, Q12, Q13, Q14, Q15, Q16, Q17, Q18, Q19, Q20, Q21, Q22, Q23]), "operationType" : NewBodyOperationType.ADD, "depth" : 3 * mm, "offsetDistance" : 25 * mm});
        }
    });
